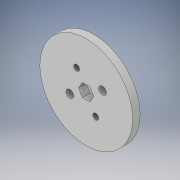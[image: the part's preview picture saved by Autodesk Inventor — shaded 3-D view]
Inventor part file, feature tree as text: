
AUTODESK INVENTOR PART (.ipt)
format: ipt  version: 2017 (Build 210142000, 142)  size: 249,344 bytes
history: native  units: in
note: dims shown in document units (in); Inventor stores cm internally (conversion verified against a paired STEP export)
features: sketch x9, thicken_offset x9, extrude x7, hole x2, pattern_circular x1
ambient origin geometry x8: Origin, YZ Plane, XZ Plane, XY Plane, X Axis, Y Axis, Z Axis, Center Point
bodies: Solid1 (feature_tree)
feature tree (28):
  extrude  "Extrusion1"  Depth=0.125in TaperAngle=0.0deg
  extrude  "Extrusion2"  TaperAngle=120.0deg  [1 undecoded]
  pattern_circular  "Circular Pattern1"  [2 undecoded]
  extrude  "Extrusion3"  Depth=0.125in
  sketch  "Sketch5"  dims[d7=0.3236in]
  extrude  "Extrusion4"  Depth=0.125in
  hole  "Hole2"  [1 undecoded]
  extrude  "Extrusion5"  Depth=0.125in TaperAngle=0.0deg
  extrude  "Extrusion6"  Depth=0.125in TaperAngle=360.0deg
  thicken_offset  "Thicken1"
  thicken_offset  "Thicken2"
  thicken_offset  "Thicken3"
  thicken_offset  "Thicken4"
  thicken_offset  "Thicken5"
  thicken_offset  "Thicken6"
  thicken_offset  "Thicken7"
  thicken_offset  "Thicken8"
  thicken_offset  "Thicken9"
  hole  "Hole5"  [1 undecoded]
  sketch  "Sketch15"  dims[d12=0.489in]
  extrude  "Extrusion9"  Depth=0.125in
  sketch  "Sketch1"  dims[d0=2.176in d1=0.125in d2=0.0in]
  sketch  "Sketch2"  dims[d3=120.0deg d5=120.0deg]
  sketch  "Sketch4"  dims[d6=120.0deg]
  sketch  "Sketch7"  dims[d8=0.2in]
  sketch  "Sketch8"  dims[d9=0.2in]
  sketch  "Sketch14"  dims[d11=0.7479in]
  sketch  "Sketch16"  dims[d13=0.323in d14=0.199in d15=0.199in d16=0.0423in d17=0.021in d18=0.125in d19=0.0in d20=1.1811in d21=360.0deg d49=1.0in d50=0.0in d51=0.02in d52=0.9375in d54=0.17in d55=0.9375in d57=0.17in d58=0.9375in d60=0.17in d61=0.9375in d63=0.17in d64=0.9375in d66=0.17in d67=1.0in d68=0.0in d69=0.9375in d70=0.938in d82=0.235in d86=0.4118in d88=0.935in d89=1.2386in d90=0.17in d91=0.75in d92=0.375in d93=0.25in d94=0.5635in d95=1.0in d96=0.8108in d105=0.205in d106=0.2077in d107=0.1287in d108=1.0in d109=0.0in d112=0.205in d113=0.1287in d114=1.0in d115=0.0in d116=0.025in d117=0.025in d118=0.025in d119=0.025in d120=0.025in d121=0.025in d122=0.025in d123=0.025in d124=0.025in d125=0.025in d126=0.025in d127=0.025in d128=0.015in d129=0.015in d130=0.015in d131=0.015in d132=0.015in d133=0.015in d170=0.315in d171=0.8252in d172=0.315in d173=0.4117in d174=0.098in d175=0.25in d176=0.375in d177=0.25in d178=0.5635in d179=0.375in d180=0.8108in d181=1.0in d182=0.0in]
note: 5 required parameter values undecoded (feature->parameter linkage not recoverable at this tier; creation-order binding heuristic only, values carry confidence <= 0.55)
